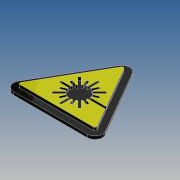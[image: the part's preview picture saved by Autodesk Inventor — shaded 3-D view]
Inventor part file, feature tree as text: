
AUTODESK INVENTOR PART (.ipt)
format: ipt  version: 2019 (Build 230136000, 136)  size: 314,880 bytes
history: native  units: mm
features: extrude x5, sketch x5, pattern_circular x2, fillet x1, projected_geometry x1
ambient origin geometry x8: Origin, YZ Plane, XZ Plane, XY Plane, X Axis, Y Axis, Z Axis, Center Point
bodies: Solid1 (feature_tree)
feature tree (14):
  extrude  "Extrusion1"  Depth=0.4mm TaperAngle=0.0deg
  fillet  "Fillet1"  Radius=1.0mm
  extrude  "Extrusion2"  Depth=0.8mm
  extrude  "Extrusion3"  Depth=0.3mm
  pattern_circular  "Circular Pattern1"  Count=8 Angle=360.0deg
  extrude  "Extrusion4"  TaperAngle=22.5deg  [1 undecoded]
  pattern_circular  "Circular Pattern2"  [2 undecoded]
  extrude  "Extrusion5"  Depth=0.4mm
  sketch  "Sketch1"  dims[d0=13.0mm d1=0.4mm d2=0.0mm d3=1.0mm]
  sketch  "Sketch2"  dims[d4=0.8mm d5=2.5mm]
  sketch  "Sketch3"  dims[d6=0.4mm d7=0.0mm d8=0.3mm]
  sketch  "Sketch4"  dims[d9=2.5mm]
  sketch  "Sketch5"  dims[d10=0.4mm d11=0.0mm d12=80.0mm d13=360.0deg d15=22.5deg d16=0.3mm d17=2.0mm d18=0.4mm d19=0.0mm d20=80.0mm d21=360.0deg d23=0.4mm d24=0.0mm]
  projected_geometry  "Project Cut Edges1"
note: 3 required parameter values undecoded (feature->parameter linkage not recoverable at this tier; creation-order binding heuristic only, values carry confidence <= 0.55)
